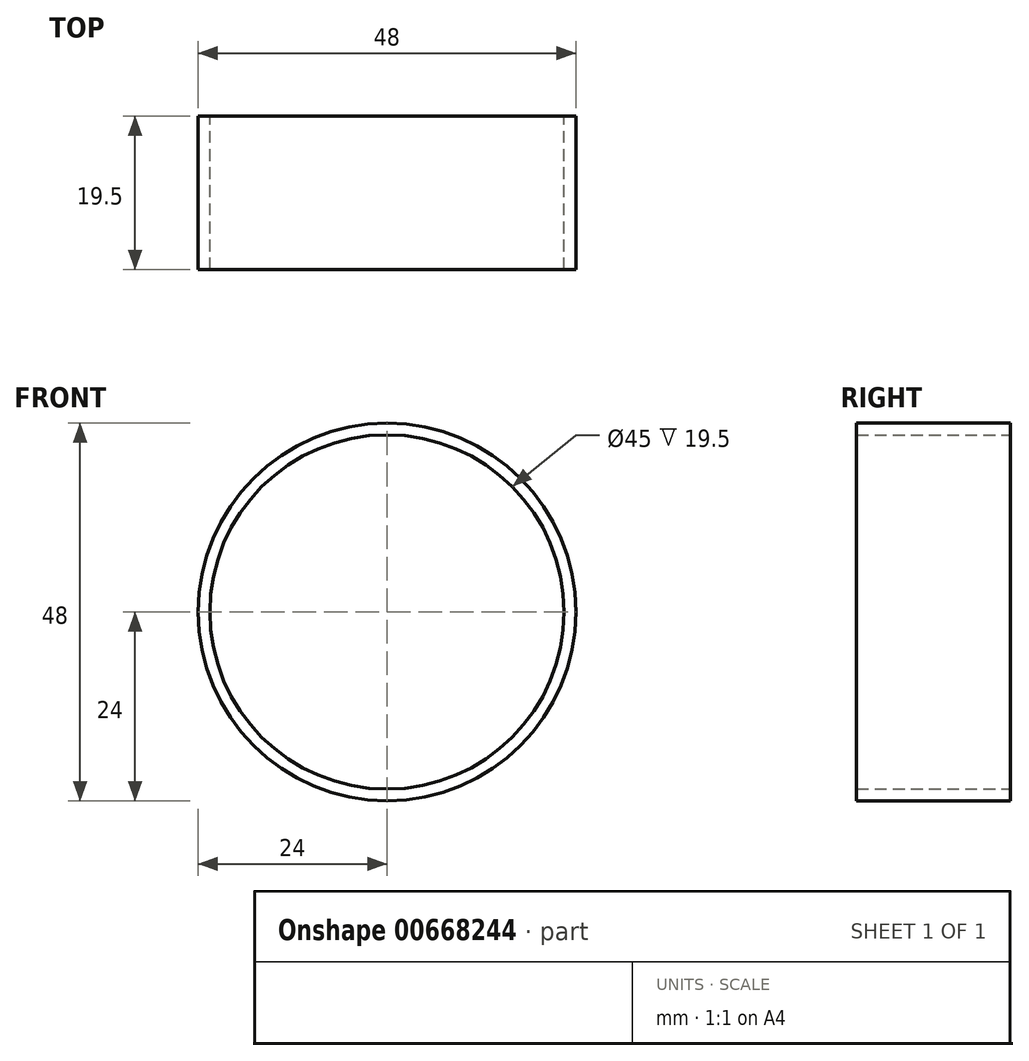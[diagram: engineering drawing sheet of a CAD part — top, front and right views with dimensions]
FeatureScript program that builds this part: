
annotation { "Feature Type Name" : "Feature", "Feature Type Description" : "" }
export const myFeature = defineFeature(function(context is Context, id is Id, definition is map)
    precondition{}
    {
        {
            var Q0;
            Q0=qCreatedBy(makeId("Front.planeOp"),FACE);
            var sketch = newSketch(context, id + "F0", { "sketchPlane" : qUnion([Q0])});
            skCircle(sketch, "E0", {"center": v(0, 0) * mm, "radius": 24 * mm});
            skCircle(sketch, "E1", {"center": v(0, 0) * mm, "radius": 22.5 * mm});
            skSolve(sketch);
        }
        {
            var Q0;
            Q0=qSketchRegion(id+"F0",true);
            extrude(context, id + "F1", {"entities" : qUnion([Q0]), "depth" : 19.5 * mm, "offsetDistance" : 25 * mm});
        }
    });
